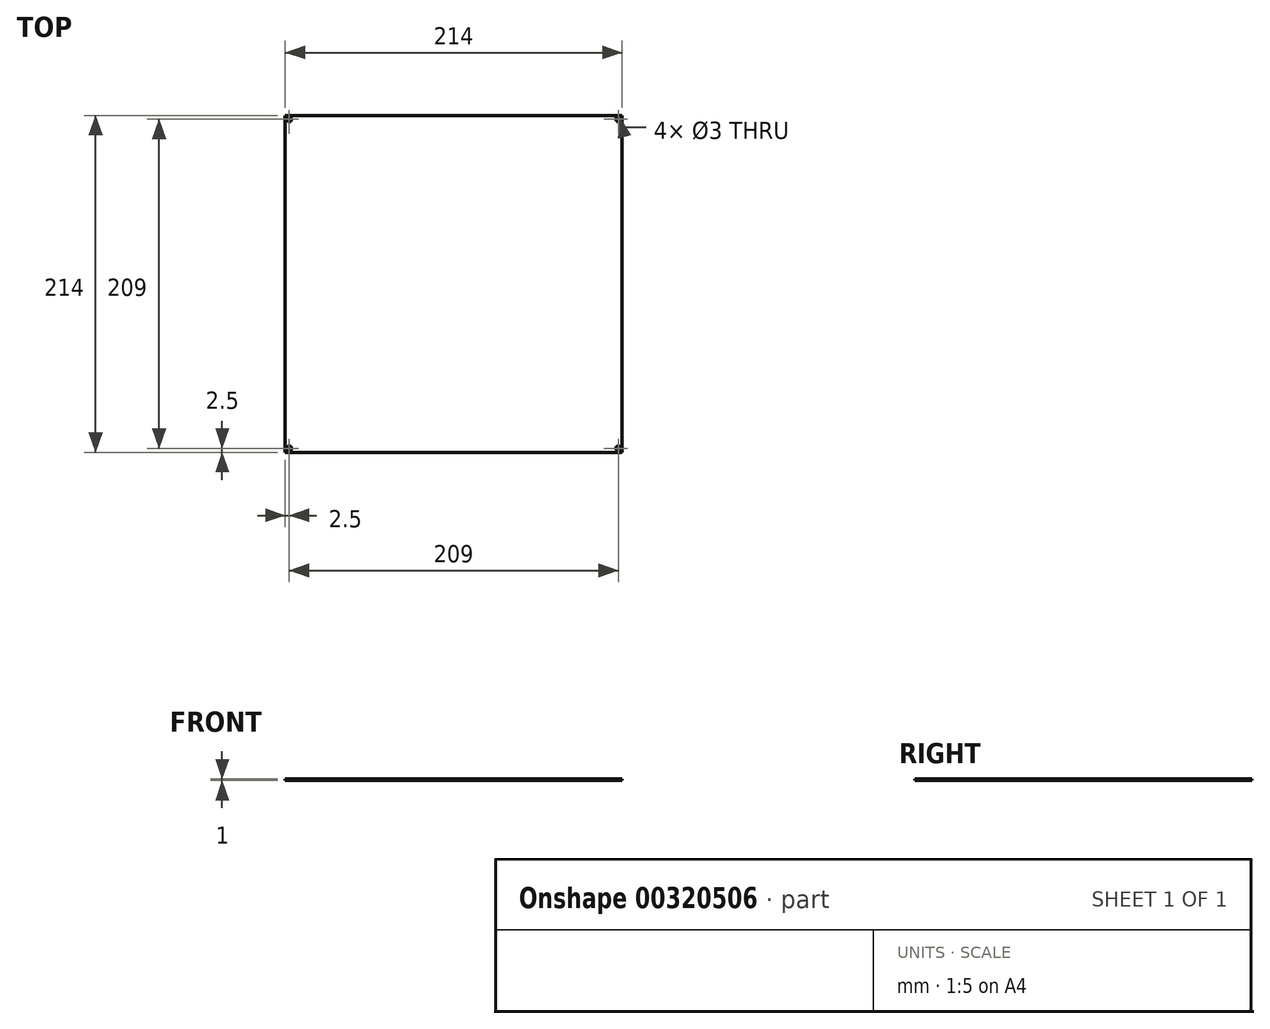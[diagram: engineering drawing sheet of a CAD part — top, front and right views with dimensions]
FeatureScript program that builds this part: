
annotation { "Feature Type Name" : "Feature", "Feature Type Description" : "" }
export const myFeature = defineFeature(function(context is Context, id is Id, definition is map)
    precondition{}
    {
        {
            var Q0;
            Q0=qCreatedBy(makeId("Top.planeOp"),FACE);
            var sketch = newSketch(context, id + "F0", { "sketchPlane" : qUnion([Q0])});
            skLineSegment(sketch, "E0.bottom", {"start": v(107, 107) * mm, "end": v(-107, 107) * mm});
            skLineSegment(sketch, "E0.top", {"start": v(107, -107) * mm, "end": v(-107, -107) * mm});
            skLineSegment(sketch, "E0.left", {"start": v(107, 107) * mm, "end": v(107, -107) * mm});
            skLineSegment(sketch, "E0.right", {"start": v(-107, 107) * mm, "end": v(-107, -107) * mm});
            skPoint(sketch, "E0.middle", {"position": v(0, 0) * mm});
            skCircle(sketch, "E1", {"center": v(-104.5, 104.5) * mm, "radius": 1.5 * mm});
            skLineSegment(sketch, "E2", {"start": v(0, -107) * mm, "end": v(0, 107) * mm, "construction": true});
            skLineSegment(sketch, "E3", {"start": v(-107, 0) * mm, "end": v(107, 0) * mm, "construction": true});
            skCircle(sketch, "E4.MirrorC", {"center": v(104.5, 104.5) * mm, "radius": 1.5 * mm});
            skCircle(sketch, "E5.MirrorC", {"center": v(-104.5, -104.5) * mm, "radius": 1.5 * mm});
            skCircle(sketch, "E6.MirrorC", {"center": v(104.5, -104.5) * mm, "radius": 1.5 * mm});
            skSolve(sketch);
        }
        {
            var Q0;
            Q0 = qSketchRegion(id + "F0", true);
            extrude(context, id + "F1", {"entities" : qUnion([Q0]), "depth" : 1 * mm});
        }
    });
